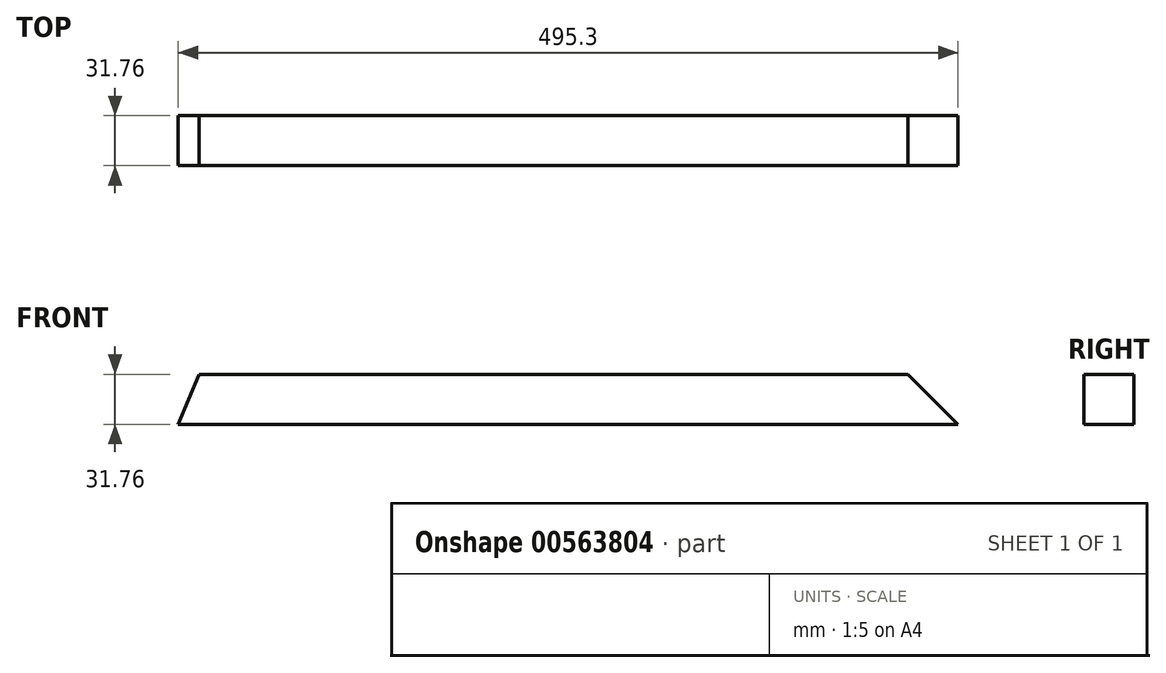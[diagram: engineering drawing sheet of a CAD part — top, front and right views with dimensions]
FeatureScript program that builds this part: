
annotation { "Feature Type Name" : "Feature", "Feature Type Description" : "" }
export const myFeature = defineFeature(function(context is Context, id is Id, definition is map)
    precondition{}
    {
        {
            var Q0;
            Q0=qCreatedBy(makeId("Front.planeOp"),FACE);
            var sketch = newSketch(context, id + "F0", { "sketchPlane" : qUnion([Q0])});
            skLineSegment(sketch, "E0.bottom", {"start": v(-247.65, 15.88) * mm, "end": v(247.65, 15.88) * mm});
            skLineSegment(sketch, "E0.top", {"start": v(-247.65, -15.88) * mm, "end": v(247.65, -15.88) * mm});
            skLineSegment(sketch, "E0.left", {"start": v(-247.65, 15.88) * mm, "end": v(-247.65, -15.88) * mm});
            skLineSegment(sketch, "E0.right", {"start": v(247.65, 15.88) * mm, "end": v(247.65, -15.88) * mm});
            skPoint(sketch, "E0.middle", {"position": v(0, 0) * mm});
            skLineSegment(sketch, "E1", {"start": v(247.65, -15.87) * mm, "end": v(215.9, 15.88) * mm});
            skSolve(sketch);
        }
        {
            var Q0;
            Q0=makeQuery(id+"F0.imprint","IMPRINT",FACE,{"disambiguationData":[TD([[makeQuery(id+"F0.imprint","IMPRINT",EDGE,{"derivedFrom":sQuery(id+"F0.wireOp",EDGE,"E0.top")}),1.0]])]});
            var sketch = newSketch(context, id + "F1", { "sketchPlane" : qUnion([Q0])});
            skLineSegment(sketch, "E2.bottom", {"start": v(-247.65, 15.88) * mm, "end": v(247.65, 15.88) * mm});
            skLineSegment(sketch, "E2.top", {"start": v(-247.65, -15.88) * mm, "end": v(247.65, -15.88) * mm});
            skLineSegment(sketch, "E2.left", {"start": v(-247.65, 15.88) * mm, "end": v(-247.65, -15.88) * mm});
            skLineSegment(sketch, "E2.right", {"start": v(247.65, 15.88) * mm, "end": v(247.65, -15.88) * mm});
            skPoint(sketch, "E2.middle", {"position": v(0, 0) * mm});
            skLineSegment(sketch, "E3", {"start": v(-247.65, -15.88) * mm, "end": v(-234.34, 15.88) * mm});
            skLineSegment(sketch, "E4", {"start": v(247.65, -15.88) * mm, "end": v(215.9, 15.88) * mm});
            skSolve(sketch);
        }
        {
            var Q0;
            Q0=makeQuery(id+"F1.imprint","IMPRINT",FACE,{"disambiguationData":[TD([[makeQuery(id+"F1.imprint","IMPRINT",EDGE,{"derivedFrom":sQuery(id+"F1.wireOp",EDGE,"E2.top")}),1.0]])]});
            extrude(context, id + "F2", {"entities" : qUnion([Q0]), "endBound" : BoundingType.SYMMETRIC, "depth" : 31.75 * mm, "offsetDistance" : 25.4 * mm});
        }
    });
